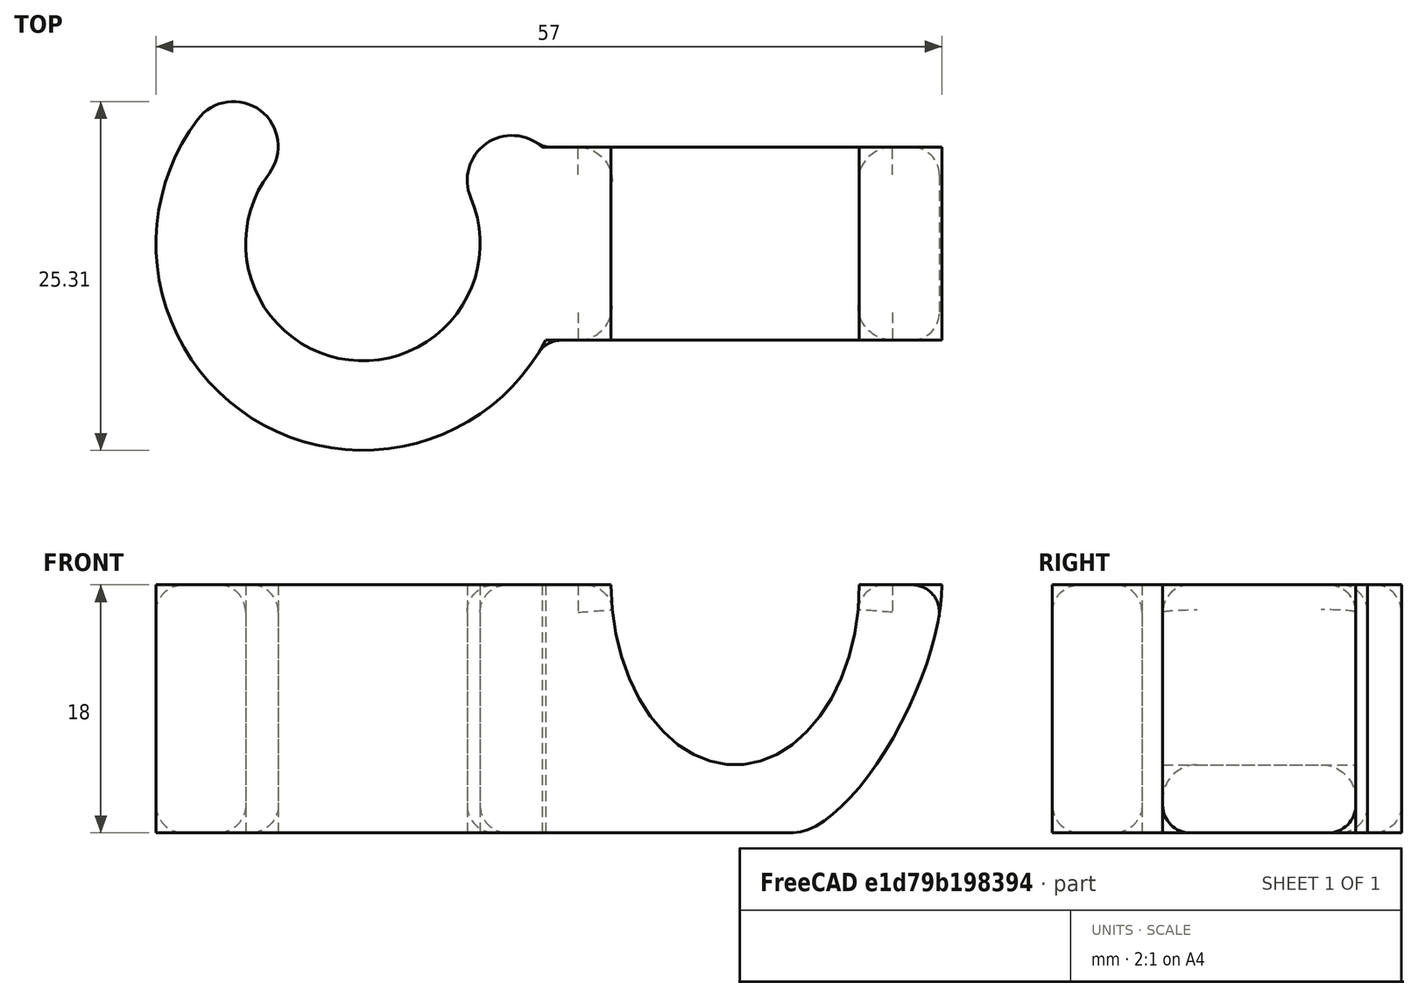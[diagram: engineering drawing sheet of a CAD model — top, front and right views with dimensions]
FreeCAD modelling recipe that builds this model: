
FCSTD DOCUMENT  (FreeCAD 0.18R4 (GitTag))
Label: dryer hook 2
License: All rights reserved
LicenseURL: http://en.wikipedia.org/wiki/All_rights_reserved
objects: Sketcher::SketchObject×2, PartDesign::Pad×2, PartDesign::Body×1, App::Part×1, Part::Fillet×1, Mesh::Feature×1
note: 8 computed .brp shape members not serialized (recipe doc carries the construction recipe); baked Part::Feature solids carry a one-line shape summary decoded from their .brp

FEATURE [Sketcher::SketchObject] Sketch
  MapMode = 5
  Support = -> [XY_Plane]
  sketch-geometry (6):
    g0: ArcOfCircle CenterX=-12 CenterY=0 CenterZ=0 NormalX=0 NormalY=0 NormalZ=1 AngleXU=0 Radius=8.5 StartAngle=2.49661 EndAngle=6.6854
    g1: ArcOfCircle CenterX=-12 CenterY=0 CenterZ=0 NormalX=0 NormalY=0 NormalZ=1 AngleXU=0 Radius=15 StartAngle=2.49661 EndAngle=6.6854
    g2: ArcOfCircle CenterX=-21.3896 CenterY=7.0639 CenterZ=0 NormalX=0 NormalY=0 NormalZ=1 AngleXU=0 Radius=3.25 StartAngle=5.6382 EndAngle=8.7798
    g3: ArcOfCircle CenterX=-1.1877 CenterY=4.59965 CenterZ=0 NormalX=0 NormalY=0 NormalZ=1 AngleXU=0 Radius=3.25 StartAngle=0.402217 EndAngle=3.54381
    g4: LineSegment [constr] StartX=-18.7924 StartY=5.11006 StartZ=0 EndX=-23.9867 EndY=9.01774 EndZ=0
    g5: LineSegment [constr] StartX=-4.17834 StartY=3.3274 StartZ=0 EndX=1.80293 EndY=5.87189 EndZ=0
  constraints (16):
    c: Radius(g0) = 8.5
    c: Radius(g1) = 15
    c: Angle(g0) = 4.18879
    c: Angle(g1) = 4.18879
    c: Coincident(g2,g1)
    c: Coincident(g3,g0)
    c: Tangent(g3,g1) = -1.5708
    c: Tangent(g2,g0) = 1.5708
    c: Coincident(g1,g0)
    c: DistanceY(g-1,g0) = 0
    c: Coincident(g4,g0)
    c: Coincident(g4,g1)
    c: Coincident(g5,g0)
    c: Coincident(g5,g1)
    c: PointOnObject(g2,g4)
    c: DistanceX(g0) = -12
FEATURE [PartDesign::Pad] Pad
  Length = 18
  Length2 = 100
  Profile = -> Sketch
  Refine = true
  Type = 0
FEATURE [Sketcher::SketchObject] Sketch001
  MapMode = 5
  Placement = pos=(0,0,0) rot=(1,0,0;1.5708rad)
  Support = -> [XZ_Plane]
  sketch-geometry (14):
    g0: LineSegment StartX=6 StartY=18 StartZ=0 EndX=0 EndY=18 EndZ=0
    g1: LineSegment StartX=0 StartY=18 StartZ=0 EndX=0 EndY=0 EndZ=0
    g2: LineSegment StartX=30 StartY=18 StartZ=0 EndX=24 EndY=18 EndZ=0
    g3: LineSegment StartX=19.236 StartY=0 StartZ=0 EndX=0 EndY=0 EndZ=0
    g4: ArcOfEllipse CenterX=23.567 CenterY=10.7574 CenterZ=0 NormalX=0 NormalY=0 NormalZ=1 MajorRadius=11.7539 MinorRadius=4.35333 AngleXU=-2.0195 StartAngle=0.176463 EndAngle=2.48587
    g5: LineSegment [constr] StartX=18.4682 StartY=0.167056 StartZ=0 EndX=28.6658 EndY=21.3478 EndZ=0
    g6: LineSegment [constr] StartX=27.4894 StartY=8.86899 StartZ=0 EndX=19.6446 EndY=12.6459 EndZ=0
    g7: GeomPoint X=18.8308 Y=0.920211 Z=0
    g8: GeomPoint X=28.3032 Y=20.5947 Z=0
    g9: ArcOfEllipse CenterX=15 CenterY=18 CenterZ=0 NormalX=0 NormalY=0 NormalZ=1 MajorRadius=13.0671 MinorRadius=9 AngleXU=-1.5708 StartAngle=4.71239 EndAngle=7.85398
    g10: LineSegment [constr] StartX=15 StartY=4.93289 StartZ=0 EndX=15 EndY=31.0671 EndZ=0
    g11: LineSegment [constr] StartX=24 StartY=18 StartZ=0 EndX=6 EndY=18 EndZ=0
    g12: GeomPoint X=15 Y=8.52639 Z=0
    g13: GeomPoint X=15 Y=27.4736 Z=0
  constraints (21):
    c: Horizontal(g0)
    c: Coincident(g0,g1)
    c: Coincident(g1,g-1)
    c: Vertical(g1)
    c: Horizontal(g2)
    c: Equal(g2,g0)
    c: Horizontal(g3)
    c: Coincident(g3,g1)
    c: DistanceY(g2,g0) = 0
    c: DistanceY(g1,g1) = 18
    c: InternalAlignment(g5-g8 -> g4) x4
    c: Perpendicular(g4,g2) = 1.5708
    c: Equal(g2,g0)
    c: DistanceX(g0,g0) = 6
    c: Tangent(g4,g3) = 1.5708
    c: InternalAlignment(g10-g13 -> g9) x4
    c: Coincident(g11,g2)
    c: Coincident(g11,g0)
    c: DistanceX(g0,g9) = 24
    c: Coincident(g9,g2)
    c: Coincident(g0,g9)
FEATURE [PartDesign::Pad] Pad001
  BaseFeature = -> Pad
  Length = 14
  Length2 = 100
  Midplane = true
  Profile = -> Sketch001
  Refine = true
  Type = 0
FEATURE [PartDesign::Body] Body
  Group = -> [Sketch,Pad,Sketch001,Pad001]
  Origin = -> Origin
  Tip = -> Pad001
FEATURE [App::Part] Part
  Group = -> [Body]
  Origin = -> Origin001
FEATURE [Part::Fillet] Fillet
  Base = -> Pad001
  Edges = 24 edges: [Edge3 r=2,Edge4 r=2,Edge6 r=2,Edge7 r=2,Edge8 r=2,Edge9 r=2,Edge10 r=2,Edge11 r=2,Edge12 r=2,Edge13 r=2,Edge14 r=2.5,Edge15 r=2,Edge16 r=2,Edge17 r=2,Edge18 r=2,Edge19 r=2.5,Edge20 r=2,Edge21 r=2,Edge22 r=2,Edge23 r=2,Edge24 r=2,Edge25 r=2,Edge26 r=2,Edge27 r=2]
FEATURE [Mesh::Feature] Mesh  label="Fillet (Meshed)"
